# Revit family: EZ-LZ_S8WSVRL-S_K
name_source: partatom
category: Plumbing Fixtures
units: mm (PartAtom-declared; Revit-internal decimal feet)

## family parameters
Always vertical = Yes
Cut with Voids When Loaded = Yes
OmniClass Number = 23.45.00.00
OmniClass Title = Sanitary, Laundry, and Cleaning Equipment
Part Type = Normal
Room Calculation Point = No
Round Connector Dimension = Use Diameter
Shared = No
Work Plane-Based = No

## types (4) — shared parameters
Activation by = Electronic Bottle Filler Sensor with Electronic Front and Side Bubbler Pushbar
Assembly Code = D2010810
BUBBLER_MATERIAL = Metal - Steel - Stainless - Chrome
Bubbler Style = Vandal Resistant
CW Connection = Yes
Chilling Capacity = 8.0 GPH
DRAIN_MATERIAL = Metal - Steel - Stainless - Chrome
Description = Elkay EZH2O Bottle Filling Station with Single ADA Cooler, Filtered Non-Refrigerated Light Gray
Dimensions (L x W x H) = 18-3/8 inch x 19- inch x 39 1/16 inch
Drain_Pipe 1 1/2" = 38 mm
Full Load Amps = 6
HW Connection = No
Inlet_Pipe 3/8" = 10 mm  [stored 0.0328084 ft]
Installation Location = Indoor
Manufacturer = Elkay
Mounting Type = Wall Mount (On Wall)
No. of Stations Served = 1
Power = 115V/60Hz
Rated Watts = 370
SINK_MATERIAL = Metal - Steel - Stainless - Chrome
Vent Connection = No
Version = 1.0.0.0
Waste Connection = Yes

## per-type parameters (varying)
| type | Approx. Shipping Weight | Finish | Special Features |
| EZS8WSVRLK | 82 lbs | Light Gray Granite | Antimicrobial, Green Ticker™, Hands Antimicrobial, Green Ticker™, Hands Free, Laminar Flow, Real Drain |
| EZS8WSVRSK | 82 lbs | Stainless Steel | Antimicrobial, Green Ticker™, Hands Antimicrobial, Green Ticker™, Hands Free, Laminar Flow, Real Drain |
| LZS8WSVRLK | 85 lbs | Light Gray Granite | Antimicrobial, Green Ticker™, Hands Antimicrobial, Green Ticker™, Hands Free, Laminar Flow, Real Drain  Visual Filter Monitor |
| LZS8WSVRSK | 85 lbs | Stainless Steel | Antimicrobial, Green Ticker™, Hands Antimicrobial, Green Ticker™, Hands Free, Laminar Flow, Real Drain  Visual Filter Monitor |

note: column(s) folded — value = type name in every type: Model

note: [stored X ft] marks values corroborated as IEEE doubles in the binary element streams (Revit-internal decimal feet)

## geometry (parser evidence)
native form markers: Sweep x23
no freeform markers — native parametric forms only
